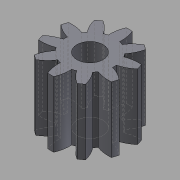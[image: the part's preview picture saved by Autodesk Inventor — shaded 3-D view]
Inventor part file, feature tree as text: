
AUTODESK INVENTOR PART (.ipt)
format: ipt  version: 2015 (Build 190159000, 159)  size: 169,984 bytes
history: native  units: in
note: dims shown in document units (in); Inventor stores cm internally (conversion verified against a paired STEP export)
features: other x13, sketch x3, plane x2
ambient origin geometry x8: Origin, YZ Plane, XZ Plane, XY Plane, X Axis, Y Axis, Z Axis, Center Point
bodies: Solid1 (feature_tree)
feature tree (18):
  other  "Spur Gear14_MIR3.ipt"
  other  "Solid1::Spur Gear14_MIR3.ipt"
  other  "TaggingFeature1"
  sketch  "Sketch1"  dims[d0=0.3937in]
  sketch  "Sketch2"  dims[d16=0.4724in d17=0.0in d41=0.0in d43=0.4724in d46=0.4724in d47=0.0in d48=0.0in]
  sketch  "Sketch3"
  plane  "XZ Plane_1"
  plane  "Work Plane2"
  other  "Z Axis_1"
  other  "Srf1"
  other  "Srf1::Derived"
  other  "Distance iMate"
  other  "Align iMate"
  other  "Mesh iMate"
  other  "Axis iMate"
  other  "Position iMate"
  other  "Mesh iMate2"
  other  "Start plane iMate"
